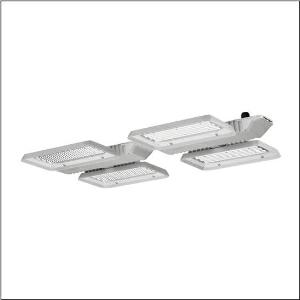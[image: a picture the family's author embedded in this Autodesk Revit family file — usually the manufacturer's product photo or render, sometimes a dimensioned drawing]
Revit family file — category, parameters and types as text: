
# Revit family: highbay_11_51hla2d24mcad
name_source: partatom
category: Lighting Fixtures
units: mm (PartAtom-declared; Revit-internal decimal feet)

## family parameters
Cut with Voids When Loaded = No
Host = Face
Light Source = No
Part Type = Normal
Room Calculation Point = No
Round Connector Dimension = Use Diameter
Shared = No

## types (1)
- --- (1 x LED, 4320 lm, 28.2 W, 4000K)
    Apparent Load = 28 VA
    CIE Flux Codes = 89 96 99 100 100
    Color Rendering = 80
    Color Temperature = 4000K
    Default Elevation = 1800 mm
    Description = Highbay 11, LED high bay luminaire, primary light control with lens, of PMMA, light emission: direct distribution, primary light characteristic: symmetric, installation type: suspended mounting, surface-mounted, for 2x 2x LED, rated luminous flux: 28.800lm, luminous efficacy: 177lm/W, light colour: 840, colour temperature: 4000K, control gear: ECG DALI, with terminal, 5-pole, max. 2.5mm², mains connection: 230..240V, AC/DC, 50/60Hz, rated input power: 162W, LED unit, of diecast aluminium, bead blasted, unplated, silver, length: 940mm, width: 500mm, height: 65mm, housing, of diecast aluminium, bead blasted, uncoated, silver, protection rating (complete): IP65, insulation class (complete): insulation class I (protective earthing), certification: CE, UKCA, protection symbol: D, impact resistance: IK08 with glass or PC cover, permissible operating ambient temperature: -35..+55°C, standard: EN 60598-2-22, reducing of maximum allowable ambient temperature of 5°C with ceiling mounting, corresponds to IFS (International Featured Standards) requirements for safety and quality in the food industry, packaging unit: 1 piece
    Height = 95 mm
    Lamp = 1 x LED
    Lamp Light Flux = 4320 lm
    Lamp Power = 28.2 W
    Lamp count = 1
    Length = 939 mm
    Luminous efficacy = 153 lm/W
    Manufacturer = Siteco
    ModVariant = No
    Model = 51HLA2D24MCAD
    Mounting Place = Ceiling
    Mounting Type = Pendant
    Number of Poles = 1
    OnlyDefault = Yes
    Power Factor = 1
    Product Name = Highbay 11
    Product group = LED high bay luminaire
    ProductGroupID = 903
    Protection Class = Protection class I
    Protection Degree = IP 65
    RLX_Detail_Level = 1
    RLX_Emergency_Light_Flux = 0 lm
    RLX_Emergency_Type = 0
    RLX_Emergency_Type_DB = No
    RlxData = <blob elided: 104601 chars, md5=41407c32>
    Socket = socket
    Standby Power = 0 W
    System Light Flux = 4320 lm
    System Power = 28 W
    Type Comments = : central accumulator DC – ECG emengency level 15%
    Type Image = l_1003428.jpg
    URL = http://relux.com
    VarID = @adj_135355
    Voltage = 0 V
    Weight = 0.00 kg
    Width = 501 mm

## geometry (parser evidence)
native form markers: Blend x4, Sweep x12
no freeform markers — native parametric forms only
